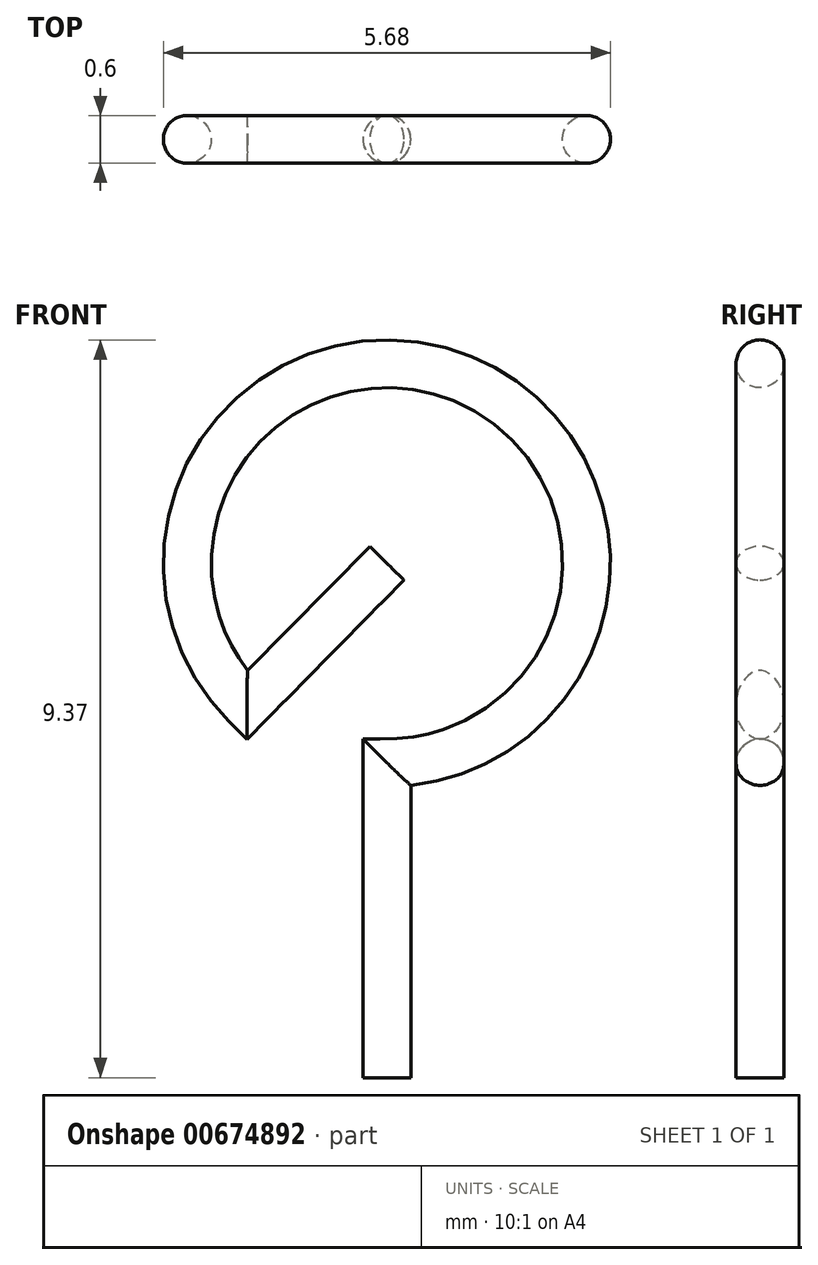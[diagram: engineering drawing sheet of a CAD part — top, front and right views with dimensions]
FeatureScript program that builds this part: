
annotation { "Feature Type Name" : "Feature", "Feature Type Description" : "" }
export const myFeature = defineFeature(function(context is Context, id is Id, definition is map)
    precondition{}
    {
        {
            var Q0;
            Q0=qCreatedBy(makeId("Front.planeOp"),FACE);
            var sketch = newSketch(context, id + "F0", { "sketchPlane" : qUnion([Q0])});
            skLineSegment(sketch, "E0", {"start": v(0, 0) * mm, "end": v(0, 4) * mm});
            skArc(sketch, "E1", {"start": v(0, 4) * mm, "mid": v(0.96, 8.88) * mm, "end": v(-1.78, 4.73) * mm});
            skLineSegment(sketch, "E2", {"start": v(0, 6.54) * mm, "end": v(-1.78, 4.73) * mm});
            skSolve(sketch);
        }
        {
            var Q0;
            Q0=qCreatedBy(makeId("Top.planeOp"),FACE);
            var sketch = newSketch(context, id + "F1", { "sketchPlane" : qUnion([Q0])});
            skCircle(sketch, "E3", {"center": v(0, 0) * mm, "radius": 0.3 * mm});
            skSolve(sketch);
        }
        {
            var Q0;
            Q0=makeQuery(id+"F1.imprint","IMPRINT",FACE,{"disambiguationData":[TD([[makeQuery(id+"F1.imprint","IMPRINT",EDGE,{"derivedFrom":sQuery(id+"F1.wireOp",EDGE,"E3")}),1.0]])]});
            var Q1;
            Q1=sQuery(id+"F0.wireOp",EDGE,"E2");
            var Q2;
            Q2=sQuery(id+"F0.wireOp",EDGE,"E1");
            var Q3;
            Q3=sQuery(id+"F0.wireOp",EDGE,"E0");
            sweep(context, id + "F2", {"profiles" : qUnion([Q0]), "path" : qUnion([Q1, Q2, Q3])});
        }
    });
